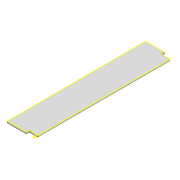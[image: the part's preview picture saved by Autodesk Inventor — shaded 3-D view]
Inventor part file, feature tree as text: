
AUTODESK INVENTOR PART (.ipt)
format: ipt  version: 2022 (Build 260153000, 153)  size: 113,664 bytes
history: native  units: mm
features: sketch x4, extrude x3, pattern_linear x1, plane x1, mirror x1, projected_geometry x1
ambient origin geometry x8: Origin, YZ Plane, XZ Plane, XY Plane, X Axis, Y Axis, Z Axis, Center Point
bodies: Solid1 (feature_tree)
feature tree (11):
  extrude  "Extrusion1"  Depth=100.0mm
  extrude  "Extrusion2"  Depth=6.0mm
  pattern_linear  "Rectangular Pattern1"  Spacing1=10.0mm  [1 undecoded]
  plane  "Work Plane1"
  extrude  "Extrusion3"  Depth=6.0mm
  mirror  "Mirror1"
  sketch  "Sketch4"  dims[d6=10.0mm d7=10.0mm d8=0.0mm d9=30.0mm d11=6.0mm d12=11.0mm d13=31.0mm d14=10.0mm d15=0.0mm]
  sketch  "Sketch1"  dims[d0=500.0mm d1=100.0mm]
  sketch  "Sketch2"  dims[d2=6.0mm d3=0.0mm d4=2.95mm]
  sketch  "Sketch3"  dims[d5=5.0mm]
  projected_geometry  "Projected Loop1"
note: 1 required parameter value undecoded (feature->parameter linkage not recoverable at this tier; creation-order binding heuristic only, values carry confidence <= 0.55)
